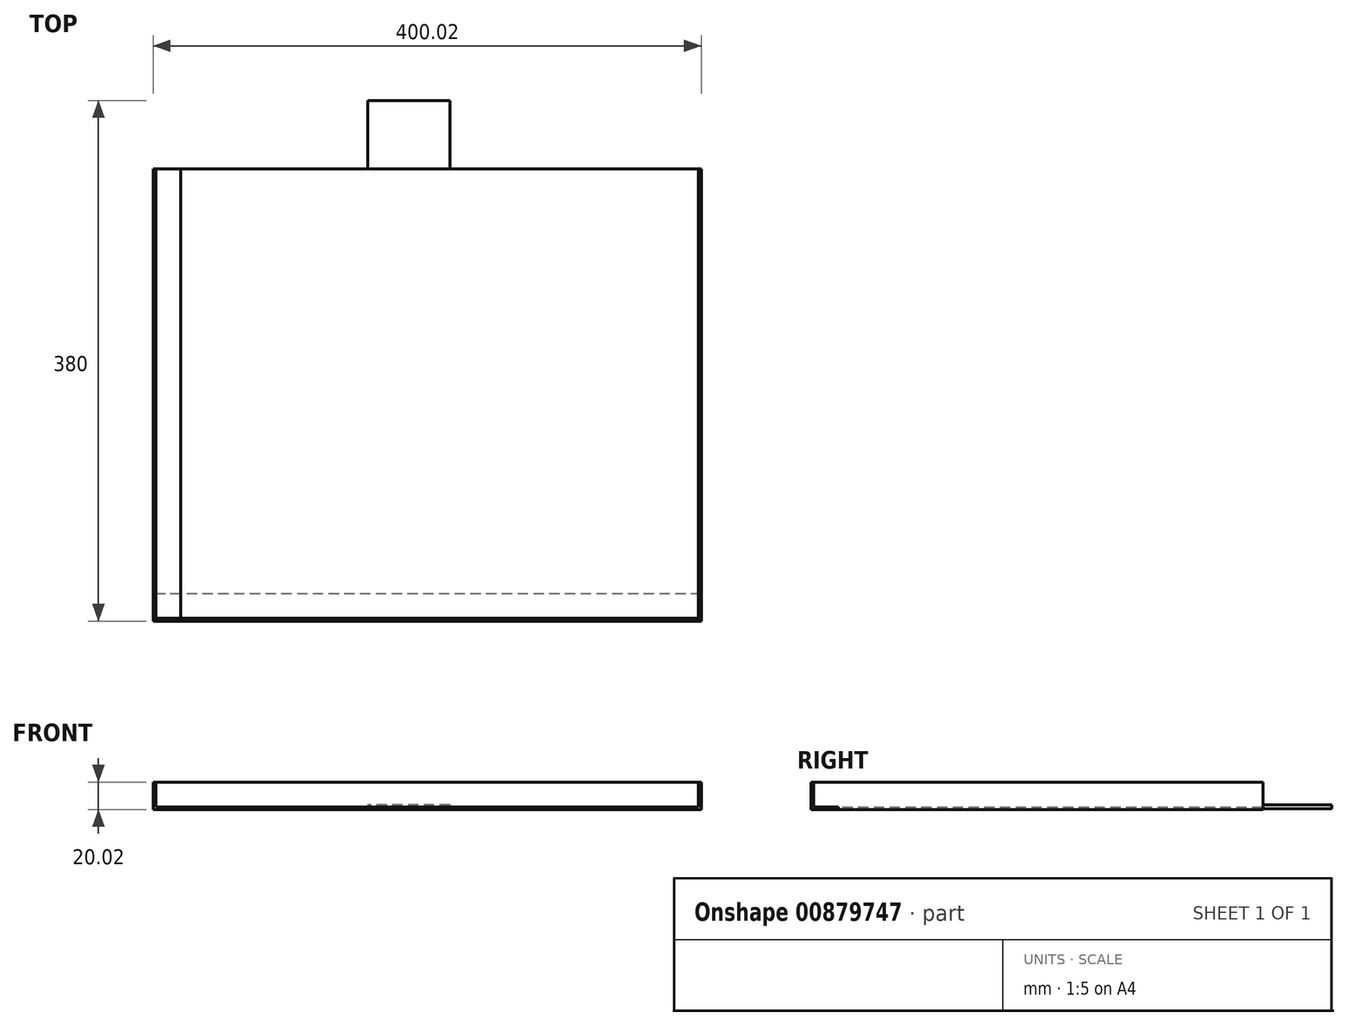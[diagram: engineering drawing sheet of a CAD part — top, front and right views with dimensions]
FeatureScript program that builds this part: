
annotation { "Feature Type Name" : "Feature", "Feature Type Description" : "" }
export const myFeature = defineFeature(function(context is Context, id is Id, definition is map)
    precondition{}
    {
        {
            var Q0;
            Q0=qCreatedBy(makeId("Top.planeOp"),FACE);
            var sketch = newSketch(context, id + "F0", { "sketchPlane" : qUnion([Q0])});
            skLineSegment(sketch, "E0.bottom", {"start": v(180, -165) * mm, "end": v(-180, -165) * mm});
            skLineSegment(sketch, "E0.top", {"start": v(180, 165) * mm, "end": v(-180, 165) * mm});
            skLineSegment(sketch, "E0.left", {"start": v(180, -165) * mm, "end": v(180, 165) * mm});
            skLineSegment(sketch, "E0.right", {"start": v(-180, -165) * mm, "end": v(-180, 165) * mm});
            skPoint(sketch, "E0.middle", {"position": v(0, 0) * mm});
            skSolve(sketch);
        }
        {
            var Q0;
            Q0 = qSketchRegion(id + "F0", true);
            extrude(context, id + "F1", {"entities" : qUnion([Q0]), "depth" : 2 * mm, "offsetDistance" : 25 * mm});
        }
        {
            var Q0;
            Q0=qCreatedBy(makeId("Front.planeOp"),FACE);
            var sketch = newSketch(context, id + "F2", { "sketchPlane" : qUnion([Q0])});
            skLineSegment(sketch, "E1", {"start": v(-180.02, 2) * mm, "end": v(-198.02, 2) * mm});
            skLineSegment(sketch, "E2", {"start": v(-198.02, 2) * mm, "end": v(-198.02, 20) * mm});
            skLineSegment(sketch, "E3", {"start": v(-198.02, 20) * mm, "end": v(-200.02, 20) * mm});
            skLineSegment(sketch, "E4", {"start": v(-200.02, 20) * mm, "end": v(-200.02, 0) * mm});
            skLineSegment(sketch, "E5", {"start": v(-200.02, 0) * mm, "end": v(-180.02, 0) * mm});
            skLineSegment(sketch, "E6", {"start": v(-180.02, 0) * mm, "end": v(-180.02, 2) * mm});
            skSolve(sketch);
        }
        {
            var Q0;
            Q0 = qSketchRegion(id + "F2", true);
            extrude(context, id + "F3", {"entities" : qUnion([Q0]), "operationType" : NewBodyOperationType.ADD, "endBound" : BoundingType.SYMMETRIC, "depth" : 330 * mm, "offsetDistance" : 25 * mm});
        }
        {
            var Q0;
            Q0=qCreatedBy(makeId("Front.planeOp"),FACE);
            var sketch = newSketch(context, id + "F4", { "sketchPlane" : qUnion([Q0])});
            skLineSegment(sketch, "E7", {"start": v(197.98, 20) * mm, "end": v(197.98, 2) * mm});
            skLineSegment(sketch, "E8", {"start": v(197.98, 2) * mm, "end": v(179.98, 2) * mm});
            skLineSegment(sketch, "E9", {"start": v(179.98, 2) * mm, "end": v(179.98, 0) * mm});
            skLineSegment(sketch, "E10", {"start": v(179.98, 0) * mm, "end": v(199.98, 0) * mm});
            skLineSegment(sketch, "E11", {"start": v(199.98, 0) * mm, "end": v(199.98, 20) * mm});
            skLineSegment(sketch, "E12", {"start": v(199.98, 20) * mm, "end": v(197.98, 20) * mm});
            skSolve(sketch);
        }
        {
            var Q0;
            Q0 = qSketchRegion(id + "F4", true);
            extrude(context, id + "F5", {"entities" : qUnion([Q0]), "operationType" : NewBodyOperationType.ADD, "endBound" : BoundingType.SYMMETRIC, "depth" : 330 * mm, "offsetDistance" : 25 * mm});
        }
        {
            var Q0;
            Q0=qCreatedBy(makeId("Right.planeOp"),FACE);
            var sketch = newSketch(context, id + "F6", { "sketchPlane" : qUnion([Q0])});
            skLineSegment(sketch, "E13", {"start": v(3359.28, -196.08) * mm, "end": v(3341.28, -196.08) * mm});
            skLineSegment(sketch, "E14", {"start": v(3341.28, -196.08) * mm, "end": v(3341.28, -178.08) * mm});
            skLineSegment(sketch, "E15", {"start": v(3341.28, -178.08) * mm, "end": v(3339.28, -178.08) * mm});
            skLineSegment(sketch, "E16", {"start": v(3339.28, -178.08) * mm, "end": v(3339.28, -198.08) * mm});
            skLineSegment(sketch, "E17", {"start": v(3339.28, -198.08) * mm, "end": v(3359.28, -198.08) * mm});
            skLineSegment(sketch, "E18", {"start": v(3359.28, -198.08) * mm, "end": v(3359.28, -196.08) * mm});
            skLineSegment(sketch, "E19", {"start": v(-145, 2) * mm, "end": v(-163, 2) * mm});
            skLineSegment(sketch, "E20", {"start": v(-163, 2) * mm, "end": v(-163, 20) * mm});
            skLineSegment(sketch, "E21", {"start": v(-163, 20) * mm, "end": v(-165, 20) * mm});
            skLineSegment(sketch, "E22", {"start": v(-165, 20) * mm, "end": v(-165, 0) * mm});
            skLineSegment(sketch, "E23", {"start": v(-165, 0) * mm, "end": v(-145, 0) * mm});
            skLineSegment(sketch, "E24", {"start": v(-145, 0) * mm, "end": v(-145, 2) * mm});
            skSolve(sketch);
        }
        {
            var Q0;
            Q0=makeQuery(id+"F6.imprint","IMPRINT",FACE,{"disambiguationData":[TD([[makeQuery(id+"F6.imprint","IMPRINT",EDGE,{"derivedFrom":sQuery(id+"F6.wireOp",EDGE,"E19")}),1.0]])]});
            extrude(context, id + "F7", {"entities" : qUnion([Q0]), "endBound" : BoundingType.SYMMETRIC, "depth" : 400 * mm, "offsetDistance" : 25 * mm});
        }
        {
            var Q0;
            Q0=qCreatedBy(makeId("Right.planeOp"),FACE);
            var sketch = newSketch(context, id + "F8", { "sketchPlane" : qUnion([Q0])});
            skLineSegment(sketch, "E25", {"start": v(162.97, 20.08) * mm, "end": v(162.97, 2.08) * mm});
            skLineSegment(sketch, "E26", {"start": v(162.97, 2.08) * mm, "end": v(144.97, 2.08) * mm});
            skLineSegment(sketch, "E27", {"start": v(144.97, 2.08) * mm, "end": v(144.97, 0.08) * mm});
            skLineSegment(sketch, "E28", {"start": v(144.97, 0.08) * mm, "end": v(164.97, 0.08) * mm});
            skLineSegment(sketch, "E29", {"start": v(164.97, 0.08) * mm, "end": v(164.97, 20.08) * mm});
            skLineSegment(sketch, "E30", {"start": v(164.97, 20.08) * mm, "end": v(162.97, 20.08) * mm});
            skSolve(sketch);
        }
        {
            var Q0;
            Q0=sQuery(id+"F8.wireOp",EDGE,"E25");
            var Q1;
            Q1=sQuery(id+"F8.wireOp",EDGE,"E28");
            var Q2;
            Q2=sQuery(id+"F8.wireOp",EDGE,"E27");
            var Q3;
            Q3=sQuery(id+"F8.wireOp",EDGE,"E26");
            var Q4;
            Q4=sQuery(id+"F8.wireOp",EDGE,"E30");
            var Q5;
            Q5=sQuery(id+"F8.wireOp",EDGE,"E29");
            extrude(context, id + "F9", {"bodyType" : ToolBodyType.SURFACE, "surfaceEntities" : qUnion([Q0, Q1, Q2, Q3, Q4, Q5]), "endBound" : BoundingType.SYMMETRIC, "depth" : 400 * mm, "offsetDistance" : 25 * mm});
        }
        {
            var Q0;
            Q0=makeQuery(id+"F1.opExtrude","CAP_FACE",FACE,{"disambiguationData":[OSD([sQuery(id+"F0.wireOp",EDGE,"E0.bottom"),sQuery(id+"F0.wireOp",EDGE,"E0.top"),sQuery(id+"F0.wireOp",EDGE,"E0.left"),sQuery(id+"F0.wireOp",EDGE,"E0.right")])],"isStart":false});
            var sketch = newSketch(context, id + "F10", { "sketchPlane" : qUnion([Q0])});
            skLineSegment(sketch, "E31.bottom", {"start": v(16.44, 165) * mm, "end": v(-43.56, 165) * mm});
            skLineSegment(sketch, "E31.top", {"start": v(16.44, 215) * mm, "end": v(-43.56, 215) * mm});
            skLineSegment(sketch, "E31.left", {"start": v(16.44, 165) * mm, "end": v(16.44, 215) * mm});
            skLineSegment(sketch, "E31.right", {"start": v(-43.56, 165) * mm, "end": v(-43.56, 215) * mm});
            skSolve(sketch);
        }
        {
            var Q0;
            Q0 = qSketchRegion(id + "F10", true);
            var Q1;
            Q1 = qConstructionFilter(qBodyType(qCreatedBy(id + "F10" ,EDGE), BodyType.WIRE), ConstructionObject.NO);
            extrude(context, id + "F11", {"entities" : qUnion([Q0]), "surfaceEntities" : qUnion([Q1]), "endBound" : BoundingType.SYMMETRIC, "depth" : 3 * mm, "offsetDistance" : 25 * mm});
        }
    });
